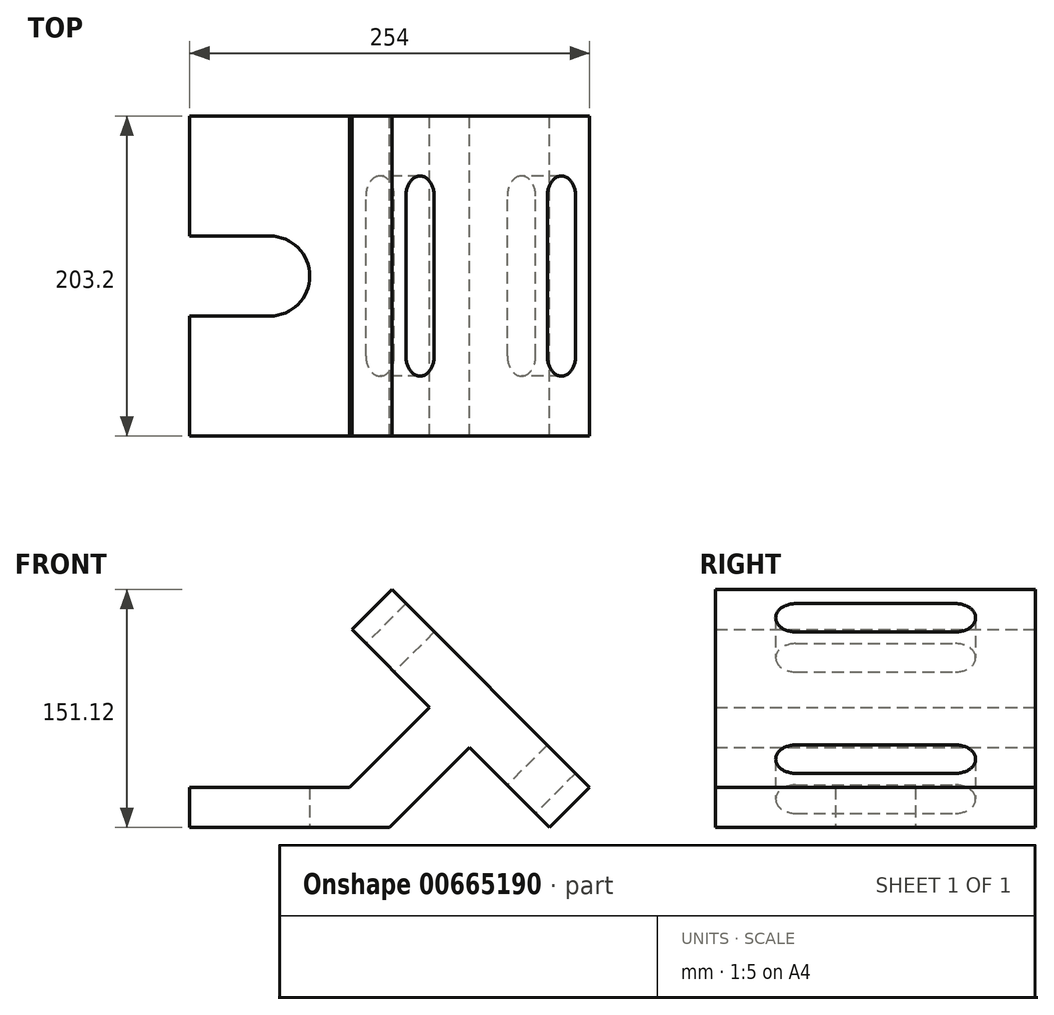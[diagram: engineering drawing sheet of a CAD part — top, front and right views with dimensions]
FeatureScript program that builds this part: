
annotation { "Feature Type Name" : "Feature", "Feature Type Description" : "" }
export const myFeature = defineFeature(function(context is Context, id is Id, definition is map)
    precondition{}
    {
        {
            var Q0;
            Q0=qCreatedBy(makeId("Top.planeOp"),FACE);
            var sketch = newSketch(context, id + "F0", { "sketchPlane" : qUnion([Q0])});
            skLineSegment(sketch, "E0", {"start": v(0, 0) * mm, "end": v(127, 0) * mm});
            skLineSegment(sketch, "E1", {"start": v(127, 0) * mm, "end": v(127, 203.2) * mm});
            skLineSegment(sketch, "E2", {"start": v(127, 203.2) * mm, "end": v(0, 203.2) * mm});
            skLineSegment(sketch, "E3", {"start": v(0, 203.2) * mm, "end": v(0, 127) * mm});
            skLineSegment(sketch, "E4", {"start": v(0, 127) * mm, "end": v(50.8, 127) * mm});
            skLineSegment(sketch, "E5", {"start": v(50.8, 76.2) * mm, "end": v(0, 76.2) * mm});
            skLineSegment(sketch, "E6", {"start": v(0, 76.2) * mm, "end": v(0, 0) * mm});
            skArc(sketch, "E7", {"start": v(50.8, 76.2) * mm, "mid": v(76.2, 101.6) * mm, "end": v(50.8, 127) * mm});
            skSolve(sketch);
        }
        {
            var Q0;
            Q0=makeQuery(id+"F0.imprint","IMPRINT",FACE,{"disambiguationData":[TD([[makeQuery(id+"F0.imprint","IMPRINT",EDGE,{"derivedFrom":sQuery(id+"F0.wireOp",EDGE,"E0")}),1.0]])]});
            extrude(context, id + "F1", {"entities" : qUnion([Q0]), "endBound" : BoundingType.SYMMETRIC, "depth" : 25.4 * mm, "offsetDistance" : 25.4 * mm});
        }
        {
            var Q0;
            Q0=makeQuery(id+"F1.opExtrude","CAP_EDGE",EDGE,{"disambiguationData":[OSD([sQuery(id+"F0.wireOp",EDGE,"E1")])],"isStart":false});
            chamfer(context, id + "F2", {"entities" : qUnion([Q0]), "width" : 25.4 * mm, "tangentPropagation" : true});
        }
        {
            var Q0;
            Q0=makeQuery(id+"F2.opChamfer","BLEND_FACE",FACE,{"disambiguationData":[OSD([sQuery(id+"F0.wireOp",EDGE,"E1")])]});
            extrude(context, id + "F3", {"entities" : qUnion([Q0]), "operationType" : NewBodyOperationType.ADD, "depth" : 71.84 * mm, "offsetDistance" : 25.4 * mm});
        }
        {
            var Q0;
            Q0=makeQuery(id+"F3.opExtrude","CAP_FACE",FACE,{"disambiguationData":[OSD([sQuery(id+"F0.wireOp",EDGE,"E1")])],"isStart":false});
            var sketch = newSketch(context, id + "F4", { "sketchPlane" : qUnion([Q0])});
            skLineSegment(sketch, "E8.bottom", {"start": v(0, -170.62) * mm, "end": v(203.2, -170.62) * mm});
            skLineSegment(sketch, "E8.top", {"start": v(0, 7.18) * mm, "end": v(203.2, 7.18) * mm});
            skLineSegment(sketch, "E8.left", {"start": v(0, -170.62) * mm, "end": v(0, 7.18) * mm});
            skLineSegment(sketch, "E8.right", {"start": v(203.2, -170.62) * mm, "end": v(203.2, 7.18) * mm});
            skLineSegment(sketch, "E9", {"start": v(50.8, -132.52) * mm, "end": v(152.4, -132.52) * mm});
            skLineSegment(sketch, "E10", {"start": v(50.8, -157.92) * mm, "end": v(152.4, -157.92) * mm});
            skArc(sketch, "E11", {"start": v(50.8, -132.52) * mm, "mid": v(38.1, -145.22) * mm, "end": v(50.8, -157.92) * mm});
            skArc(sketch, "E12", {"start": v(152.4, -157.92) * mm, "mid": v(165.1, -145.22) * mm, "end": v(152.4, -132.52) * mm});
            skLineSegment(sketch, "E13", {"start": v(50.8, -5.52) * mm, "end": v(152.4, -5.52) * mm});
            skLineSegment(sketch, "E14", {"start": v(50.8, -30.92) * mm, "end": v(152.4, -30.92) * mm});
            skArc(sketch, "E15", {"start": v(50.8, -5.52) * mm, "mid": v(38.1, -18.22) * mm, "end": v(50.8, -30.92) * mm});
            skArc(sketch, "E16", {"start": v(152.4, -30.92) * mm, "mid": v(165.1, -18.22) * mm, "end": v(152.4, -5.52) * mm});
            skSolve(sketch);
        }
        {
            var Q0;
            {var subQ0=sQuery(id+"F4.wireOp",EDGE,"E8.top");Q0=makeQuery(id+"F4.imprint","IMPRINT",FACE,{"disambiguationData":[TD([[makeQuery(id+"F4.imprint","IMPRINT",EDGE,{"derivedFrom":subQ0}),-1.0]])]});}
            var Q1;
            {var subQ10=sQuery(id+"F4.wireOp",EDGE,"E8.bottom");Q1=makeQuery(id+"F4.imprint","IMPRINT",FACE,{"disambiguationData":[TD([[makeQuery(id+"F4.imprint","IMPRINT",EDGE,{"derivedFrom":subQ10}),1.0]])]});}
            var Q2;
            {var subQ1=sQuery(id+"F0.wireOp",EDGE,"E7");var subQ2=sQuery(id+"F0.wireOp",EDGE,"E6");var subQ3=sQuery(id+"F0.wireOp",EDGE,"E5");var subQ4=sQuery(id+"F0.wireOp",EDGE,"E4");var subQ5=sQuery(id+"F0.wireOp",EDGE,"E3");var subQ6=sQuery(id+"F0.wireOp",EDGE,"E2");var subQ7=sQuery(id+"F0.wireOp",EDGE,"E1");var subQ8=sQuery(id+"F0.wireOp",EDGE,"E0");var subQ9=makeQuery(id+"F1.opExtrude","CAP_EDGE",EDGE,{"disambiguationData":[OSD([subQ7])],"isStart":false});var subQ10=makeQuery(id+"F3.opExtrude","CAP_EDGE",EDGE,{"disambiguationData":[OSD([subQ8,subQ7,subQ6,subQ5,subQ4,subQ3,subQ2,subQ1]),TDD([makeQuery(id+"F2.opChamfer","BLEND_EDGE",EDGE,{"blendedFrom":[subQ9,makeQuery(id+"F1.opExtrude","CAP_FACE",FACE,{"disambiguationData":[OSD([subQ8,subQ7,subQ6,subQ5,subQ4,subQ3,subQ2,subQ1])],"isStart":true})],"blendedInto":[makeQuery(id+"F1.opExtrude","CAP_FACE",FACE,{"disambiguationData":[OSD([subQ8,subQ7,subQ6,subQ5,subQ4,subQ3,subQ2,subQ1])],"isStart":true})]})])],"isStart":false});Q2=makeQuery(id+"F4.imprint","IMPRINT",FACE,{"disambiguationData":[TD([[makeQuery(id+"F4.imprint","IMPRINT",EDGE,{"derivedFrom":subQ10}),1.0]])]});}
            extrude(context, id + "F5", {"entities" : qUnion([Q0, Q1, Q2]), "operationType" : NewBodyOperationType.ADD, "depth" : 35.92 * mm, "offsetDistance" : 25.4 * mm});
        }
    });
